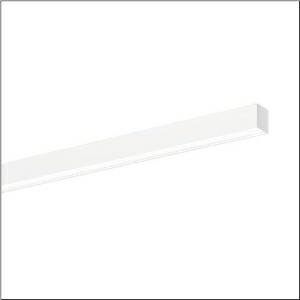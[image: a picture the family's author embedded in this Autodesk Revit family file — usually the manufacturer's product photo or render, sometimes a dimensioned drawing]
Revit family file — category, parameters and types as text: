
# Revit family: silica_21_51mx23da34wb
name_source: partatom
category: Lighting Fixtures
units: mm (PartAtom-declared; Revit-internal decimal feet)

## family parameters
Cut with Voids When Loaded = No
Host = Face
Light Source = No
Part Type = Normal
Room Calculation Point = No
Round Connector Dimension = Use Diameter
Shared = No

## types (1)
- --- (1 x LED, 3280 lm, 24.1 W, 3000K)
    Apparent Load = 24 VA
    CIE Flux Codes = 78 96 99 100 100
    Color Rendering = 80
    Color Temperature = 3000K
    Default Elevation = 1800 mm
    Description = Silica 21, office luminaire, primary optical cover: prismatic diffuser, of PMMA, CAT 2 (L<= 3000cd/m²), light emission: direct distribution, primary light characteristic: symmetric, installation type: surface-mounted, LED, rated luminous flux: 3.280lm, luminous efficacy: 136lm/W, light colour: 830, colour temperature: 3000K, control gear: DALI 2, with terminal, 3+2-pole, max. 2.5mm², mains connection: 220..240V, AC, 50/60Hz, rated input power: 24.1W, luminaire housing, of aluminium, traffic white (RAL 9016), length: 1.204mm, width: 53mm, height: 53mm, protection rating (complete): IP20, insulation class (complete): insulation class I (protective earthing), certification: CE, permissible operating ambient temperature: 0..+35°C, standard: EN 50419, packaging unit: 1 piece
    Height = 53 mm
    Lamp = 1 x LED
    Lamp Light Flux = 3280 lm
    Lamp Power = 24.1 W
    Lamp count = 1
    Length = 1204 mm
    Luminous efficacy = 136 lm/W
    Manufacturer = Siteco
    ModVariant = No
    Model = 51MX23DA34WB
    Mounting Place = Ceiling
    Mounting Type = Surface mounted
    Number of Poles = 1
    OnlyDefault = Yes
    Power Factor = 1
    Product Name = Silica 21
    Product group = office luminaire | ceiling mounted
    ProductGroupID = 301
    Protection Class = Protection class I
    Protection Degree = IP 20
    RLX_Detail_Level = 1
    RLX_Emergency_Light_Flux = 0 lm
    RLX_Emergency_Type = 0
    RLX_Emergency_Type_DB = No
    RlxData = <blob elided: 18841 chars, md5=7d84ff9a>
    Socket = socket
    Standby Power = 0 W
    System Light Flux = 3280 lm
    System Power = 24 W
    Type Comments = factory setting: luminous flux: 100 % | dim-lin: 254 | 345 mA
    Type Image = l_1335877.jpg
    URL = http://relux.com
    VarID = @adj_028245
    Voltage = 0 V
    Weight = 0.00 kg
    Width = 53 mm

## geometry (parser evidence)
native form markers: Blend x4, Sweep x11
no freeform markers — native parametric forms only
